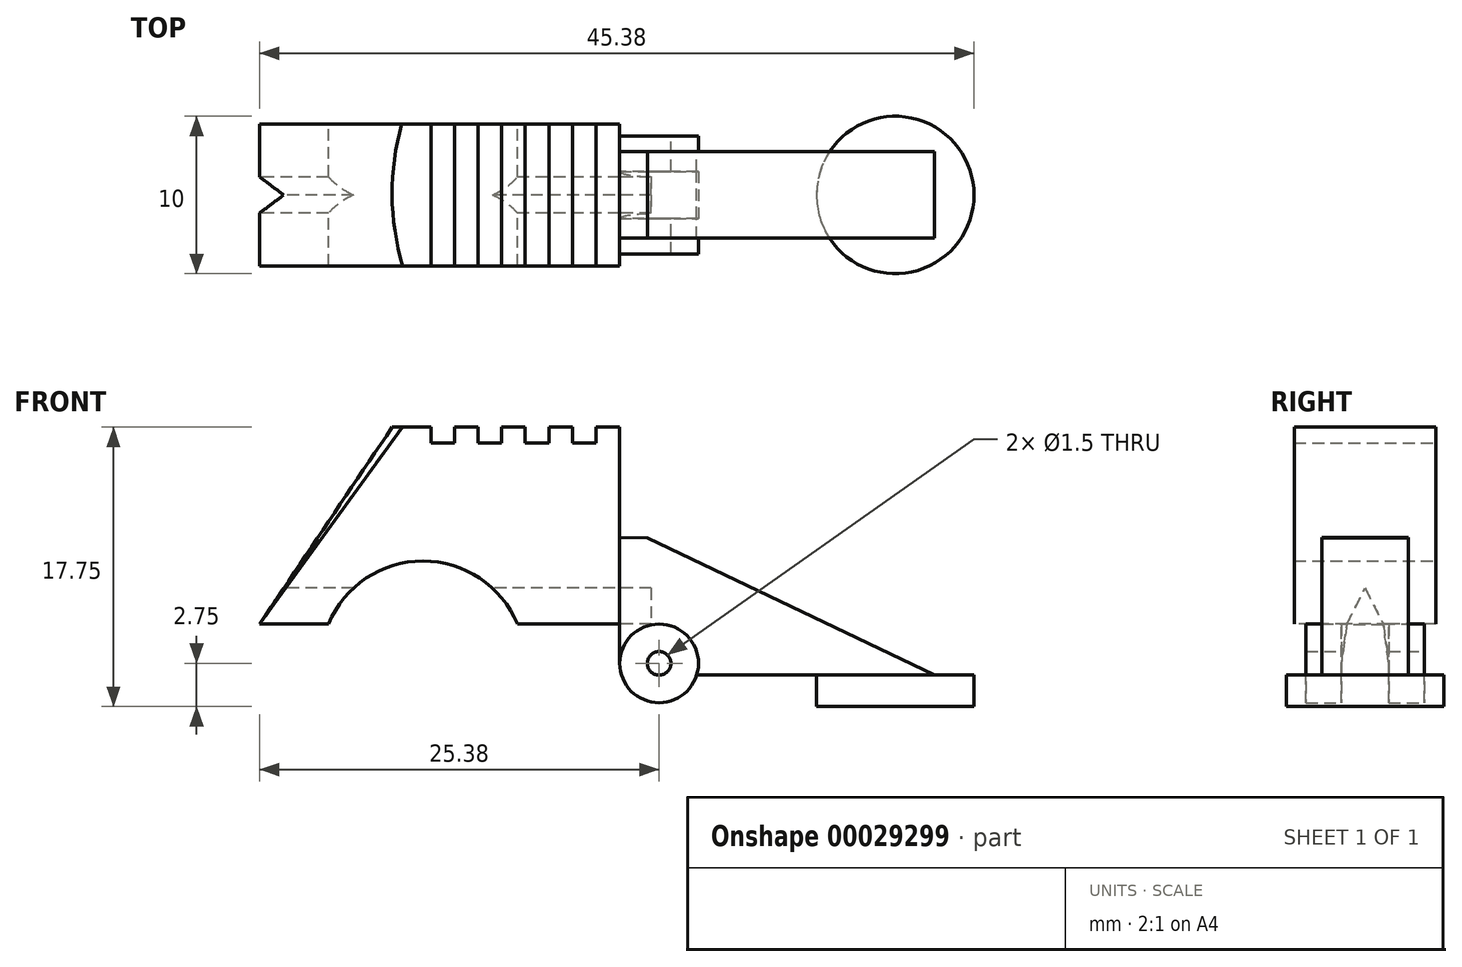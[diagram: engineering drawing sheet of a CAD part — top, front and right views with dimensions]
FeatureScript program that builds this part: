
annotation { "Feature Type Name" : "Feature", "Feature Type Description" : "" }
export const myFeature = defineFeature(function(context is Context, id is Id, definition is map)
    precondition{}
    {
        {
            var Q0;
            Q0=qCreatedBy(makeId("Front.planeOp"),FACE);
            var sketch = newSketch(context, id + "F0", { "sketchPlane" : qUnion([Q0])});
            skCircle(sketch, "E0", {"center": v(0, 0) * mm, "radius": 2.5 * mm});
            skCircle(sketch, "E1", {"center": v(0, 0) * mm, "radius": 0.75 * mm});
            skSolve(sketch);
        }
        {
            var Q0;
            Q0=qSketchRegion(id+"F0",true);
            extrude(context, id + "F1", {"entities" : qUnion([Q0]), "depth" : 3.75 * mm, "hasSecondDirection" : true, "secondDirectionOppositeDirection" : true, "secondDirectionDepth" : 3.75 * mm});
        }
        {
            var Q0;
            Q0=qCreatedBy(makeId("Front.planeOp"),FACE);
            var sketch = newSketch(context, id + "F2", { "sketchPlane" : qUnion([Q0])});
            skLineSegment(sketch, "E2", {"start": v(0, -0.75) * mm, "end": v(17.5, -0.75) * mm});
            skLineSegment(sketch, "E3", {"start": v(-2.5, 0) * mm, "end": v(-2.5, 8) * mm});
            skLineSegment(sketch, "E4", {"start": v(-0.75, 0) * mm, "end": v(-0.75, 7.97) * mm});
            skLineSegment(sketch, "E5", {"start": v(-0.75, 7.97) * mm, "end": v(17.5, -0.75) * mm});
            skLineSegment(sketch, "E6", {"start": v(-0.75, 7.97) * mm, "end": v(-2.5, 8) * mm});
            skLineSegment(sketch, "E7", {"start": v(-2.5, 0) * mm, "end": v(-0.75, 2.38) * mm});
            skLineSegment(sketch, "E8", {"start": v(-0.75, 2.38) * mm, "end": v(2.38, -0.75) * mm});
            skSolve(sketch);
        }
        {
            var Q0;
            Q0=qSketchRegion(id+"F2",true);
            extrude(context, id + "F3", {"entities" : qUnion([Q0]), "operationType" : NewBodyOperationType.ADD, "depth" : 2.75 * mm, "hasSecondDirection" : true, "secondDirectionOppositeDirection" : true, "secondDirectionDepth" : 2.75 * mm});
        }
        {
            var Q0;
            Q0=makeQuery(id+"F3.opExtrude","SWEPT_FACE",FACE,{"disambiguationData":[OSD([sQuery(id+"F2.wireOp",EDGE,"E2")])]});
            var sketch = newSketch(context, id + "F4", { "sketchPlane" : qUnion([Q0])});
            skLineSegment(sketch, "E9", {"start": v(0, 0) * mm, "end": v(15, 0) * mm});
            skCircle(sketch, "E10", {"center": v(15, 0) * mm, "radius": 5 * mm});
            skSolve(sketch);
        }
        {
            var Q0;
            Q0=qSketchRegion(id+"F4",true);
            extrude(context, id + "F5", {"entities" : qUnion([Q0]), "operationType" : NewBodyOperationType.ADD, "depth" : 2 * mm});
        }
        {
            var Q0;
            Q0=qCreatedBy(makeId("Front.planeOp"),FACE);
            var sketch = newSketch(context, id + "F6", { "sketchPlane" : qUnion([Q0])});
            skLineSegment(sketch, "E11", {"start": v(-2.5, 15) * mm, "end": v(-17, 15) * mm});
            skLineSegment(sketch, "E12", {"start": v(-2.5, 2.5) * mm, "end": v(-25.5, 2.5) * mm});
            skLineSegment(sketch, "E13", {"start": v(-2.5, 15) * mm, "end": v(-2.5, 2.5) * mm});
            skLineSegment(sketch, "E14", {"start": v(-17, 15) * mm, "end": v(-25.5, 2.5) * mm});
            skSolve(sketch);
        }
        {
            var Q0;
            Q0=qSketchRegion(id+"F6",true);
            extrude(context, id + "F7", {"entities" : qUnion([Q0]), "operationType" : NewBodyOperationType.ADD, "depth" : 4.5 * mm, "hasSecondDirection" : true, "secondDirectionOppositeDirection" : true, "secondDirectionDepth" : 4.5 * mm});
        }
        {
            var Q0;
            Q0=makeQuery(id+"F7.opExtrude","SWEPT_FACE",FACE,{"disambiguationData":[OSD([sQuery(id+"F6.wireOp",EDGE,"E11")])]});
            var sketch = newSketch(context, id + "F8", { "sketchPlane" : qUnion([Q0])});
            skLineSegment(sketch, "E15", {"start": v(-17, 4.5) * mm, "end": v(-16.34, 4.5) * mm});
            skLineSegment(sketch, "E16", {"start": v(-17, -4.5) * mm, "end": v(-16.28, -4.5) * mm});
            skLineSegment(sketch, "E17", {"start": v(-17, -4.5) * mm, "end": v(-17, 4.5) * mm});
            skArc(sketch, "E18", {"start": v(-16.34, 4.5) * mm, "mid": v(-16.96, 0) * mm, "end": v(-16.28, -4.5) * mm});
            skSolve(sketch);
        }
        {
            var Q0;
            {var subQ0=sQuery(id+"F6.wireOp",EDGE,"E12");var subQ2=sQuery(id+"F6.wireOp",EDGE,"E14");var subQ3=makeQuery(id+"F7.opExtrude","SWEPT_FACE",FACE,{"disambiguationData":[OSD([subQ2])]});Q0=makeQuery(id+"F16.boolean.opBoolean","SPLIT",FACE,{"disambiguationData":[TD([subQ3])],"derivedFrom":makeQuery(id+"F14.boolean.opBoolean","SPLIT",FACE,{"disambiguationData":[TD([makeQuery(id+"F14.opExtrude","SWEPT_FACE",FACE,{"disambiguationData":[OSD([sQuery(id+"F13.wireOp",EDGE,"E31")])]})])],"derivedFrom":makeQuery(id+"F7.opExtrude","SWEPT_FACE",FACE,{"disambiguationData":[OSD([subQ0])]})})});}
            var sketch = newSketch(context, id + "F9", { "sketchPlane" : qUnion([Q0])});
            skPoint(sketch, "E19.0", {"position": v(-25.5, -4.5) * mm});
            skLineSegment(sketch, "E20.bottom", {"start": v(-25.5, -4.5) * mm, "end": v(-25.38, -4.5) * mm});
            skLineSegment(sketch, "E20.top", {"start": v(-25.5, 4.5) * mm, "end": v(-25.38, 4.5) * mm});
            skLineSegment(sketch, "E20.left", {"start": v(-25.5, -4.5) * mm, "end": v(-25.5, 4.5) * mm});
            skLineSegment(sketch, "E20.right", {"start": v(-25.38, -4.5) * mm, "end": v(-25.38, 4.5) * mm});
            skSolve(sketch);
        }
        {
            var Q0;
            Q0=qCreatedBy(makeId("Front.planeOp"),FACE);
            var sketch = newSketch(context, id + "F10", { "sketchPlane" : qUnion([Q0])});
            skCircle(sketch, "E21", {"center": v(0, 0) * mm, "radius": 2.5 * mm});
            skSolve(sketch);
        }
        {
            var Q0;
            Q0=qSketchRegion(id+"F10",true);
            extrude(context, id + "F11", {"entities" : qUnion([Q0]), "operationType" : NewBodyOperationType.REMOVE, "oppositeDirection" : true, "depth" : 1.5 * mm, "hasSecondDirection" : true, "secondDirectionOppositeDirection" : false, "secondDirectionDepth" : 1.5 * mm});
        }
        {
            var Q0;
            Q0=makeQuery(id+"F7.opExtrude","SWEPT_FACE",FACE,{"disambiguationData":[OSD([sQuery(id+"F6.wireOp",EDGE,"E14")])]});
            var sketch = newSketch(context, id + "F12", { "sketchPlane" : qUnion([Q0])});
            skLineSegment(sketch, "E22", {"start": v(-1.15, -12.27) * mm, "end": v(0, -9.52) * mm});
            skLineSegment(sketch, "E23", {"start": v(0, -9.52) * mm, "end": v(1.15, -12.27) * mm});
            skLineSegment(sketch, "E24", {"start": v(-1.15, -12.27) * mm, "end": v(1.15, -12.27) * mm});
            skSolve(sketch);
        }
        {
            var Q0;
            Q0=makeQuery(id+"F3.opExtrude","SWEPT_FACE",FACE,{"disambiguationData":[OSD([sQuery(id+"F2.wireOp",EDGE,"E3")])]});
            var sketch = newSketch(context, id + "F13", { "sketchPlane" : qUnion([Q0])});
            skPoint(sketch, "E25.0", {"position": v(0, 4.77) * mm});
            skPoint(sketch, "E26.0", {"position": v(-1.15, 2.5) * mm});
            skPoint(sketch, "E27.0", {"position": v(1.15, 2.5) * mm});
            skPoint(sketch, "E28.0", {"position": v(-1.5, 0) * mm});
            skPoint(sketch, "E29.0", {"position": v(1.5, 0) * mm});
            skLineSegment(sketch, "E30", {"start": v(-1.5, 0) * mm, "end": v(1.5, 0) * mm});
            skLineSegment(sketch, "E31", {"start": v(1.15, 2.5) * mm, "end": v(1.5, 0) * mm});
            skLineSegment(sketch, "E32", {"start": v(1.15, 2.5) * mm, "end": v(0, 4.77) * mm});
            skLineSegment(sketch, "E33", {"start": v(0, 4.77) * mm, "end": v(-1.15, 2.5) * mm});
            skLineSegment(sketch, "E34", {"start": v(-1.15, 2.5) * mm, "end": v(-1.5, 0) * mm});
            skSolve(sketch);
        }
        {
            var Q0;
            Q0=qSketchRegion(id+"F13",true);
            extrude(context, id + "F14", {"entities" : qUnion([Q0]), "operationType" : NewBodyOperationType.REMOVE, "oppositeDirection" : true, "depth" : 2 * mm, "hasSecondDirection" : true, "secondDirectionBound" : SecondDirectionBoundingType.THROUGH_ALL, "secondDirectionOppositeDirection" : false, "secondDirectionDepth" : 25 * mm});
        }
        {
            var Q0;
            Q0=qCreatedBy(makeId("Front.planeOp"),FACE);
            var sketch = newSketch(context, id + "F15", { "sketchPlane" : qUnion([Q0])});
            skLineSegment(sketch, "E35", {"start": v(0, 0) * mm, "end": v(-15, 0) * mm});
            skCircle(sketch, "E36", {"center": v(-15, 0) * mm, "radius": 6.5 * mm});
            skSolve(sketch);
        }
        {
            var Q0;
            Q0=qSketchRegion(id+"F15",true);
            extrude(context, id + "F16", {"entities" : qUnion([Q0]), "operationType" : NewBodyOperationType.REMOVE, "endBound" : BoundingType.THROUGH_ALL, "depth" : 25 * mm, "hasSecondDirection" : true, "secondDirectionBound" : SecondDirectionBoundingType.THROUGH_ALL, "secondDirectionOppositeDirection" : true, "secondDirectionDepth" : 25 * mm});
        }
        {
            var Q1;
            Q1=qSketchRegion(id+"F9",true);
            var Q2;
            Q2=qSketchRegion(id+"F8",true);
            loft(context, id + "F17", {"operationType" : NewBodyOperationType.REMOVE, "sheetProfilesArray" : [{ "sheetProfileEntities" : qUnion([Q1]) }, { "sheetProfileEntities" : qUnion([Q2]) }]});
        }
        {
            var Q0;
            Q0=makeQuery(id+"F7.opExtrude","SWEPT_FACE",FACE,{"disambiguationData":[OSD([sQuery(id+"F6.wireOp",EDGE,"E11")])]});
            var sketch = newSketch(context, id + "F18", { "sketchPlane" : qUnion([Q0])});
            skLineSegment(sketch, "E37", {"start": v(-2.5, -4.5) * mm, "end": v(-4, -4.5) * mm});
            skLineSegment(sketch, "E38.bottom", {"start": v(-4, -4.5) * mm, "end": v(-5.5, -4.5) * mm});
            skLineSegment(sketch, "E38.top", {"start": v(-4, 4.5) * mm, "end": v(-5.5, 4.5) * mm});
            skLineSegment(sketch, "E38.left", {"start": v(-4, -4.5) * mm, "end": v(-4, 4.5) * mm});
            skLineSegment(sketch, "E38.right", {"start": v(-5.5, -4.5) * mm, "end": v(-5.5, 4.5) * mm});
            skLineSegment(sketch, "E39.1.0.0", {"start": v(-8.5, -4.5) * mm, "end": v(-8.5, 4.5) * mm});
            skLineSegment(sketch, "E39.1.0.1", {"start": v(-5.5, -4.5) * mm, "end": v(-7, -4.5) * mm});
            skLineSegment(sketch, "E39.1.0.2", {"start": v(-7, -4.5) * mm, "end": v(-7, 4.5) * mm});
            skLineSegment(sketch, "E39.1.0.3", {"start": v(-7, -4.5) * mm, "end": v(-8.5, -4.5) * mm});
            skLineSegment(sketch, "E39.1.0.4", {"start": v(-7, 4.5) * mm, "end": v(-8.5, 4.5) * mm});
            skLineSegment(sketch, "E39.2.0.0", {"start": v(-11.5, -4.5) * mm, "end": v(-11.5, 4.5) * mm});
            skLineSegment(sketch, "E39.2.0.1", {"start": v(-8.5, -4.5) * mm, "end": v(-10, -4.5) * mm});
            skLineSegment(sketch, "E39.2.0.2", {"start": v(-10, -4.5) * mm, "end": v(-10, 4.5) * mm});
            skLineSegment(sketch, "E39.2.0.3", {"start": v(-10, -4.5) * mm, "end": v(-11.5, -4.5) * mm});
            skLineSegment(sketch, "E39.2.0.4", {"start": v(-10, 4.5) * mm, "end": v(-11.5, 4.5) * mm});
            skLineSegment(sketch, "E39.direction1", {"start": v(-8.5, -4.5) * mm, "end": v(-5.5, -4.5) * mm, "construction": true});
            skLineSegment(sketch, "E40.0.3.0", {"start": v(-14.5, -4.5) * mm, "end": v(-14.5, 4.5) * mm});
            skLineSegment(sketch, "E40.3.3.0", {"start": v(-11.5, -4.5) * mm, "end": v(-13, -4.5) * mm});
            skLineSegment(sketch, "E40.6.3.0", {"start": v(-13, -4.5) * mm, "end": v(-13, 4.5) * mm});
            skLineSegment(sketch, "E40.9.3.0", {"start": v(-13, -4.5) * mm, "end": v(-14.5, -4.5) * mm});
            skLineSegment(sketch, "E40.12.3.0", {"start": v(-13, 4.5) * mm, "end": v(-14.5, 4.5) * mm});
            skSolve(sketch);
        }
        {
            var Q0;
            Q0=qSketchRegion(id+"F18",true);
            extrude(context, id + "F19", {"entities" : qUnion([Q0]), "operationType" : NewBodyOperationType.REMOVE, "oppositeDirection" : true, "depth" : 1 * mm});
        }
    });
